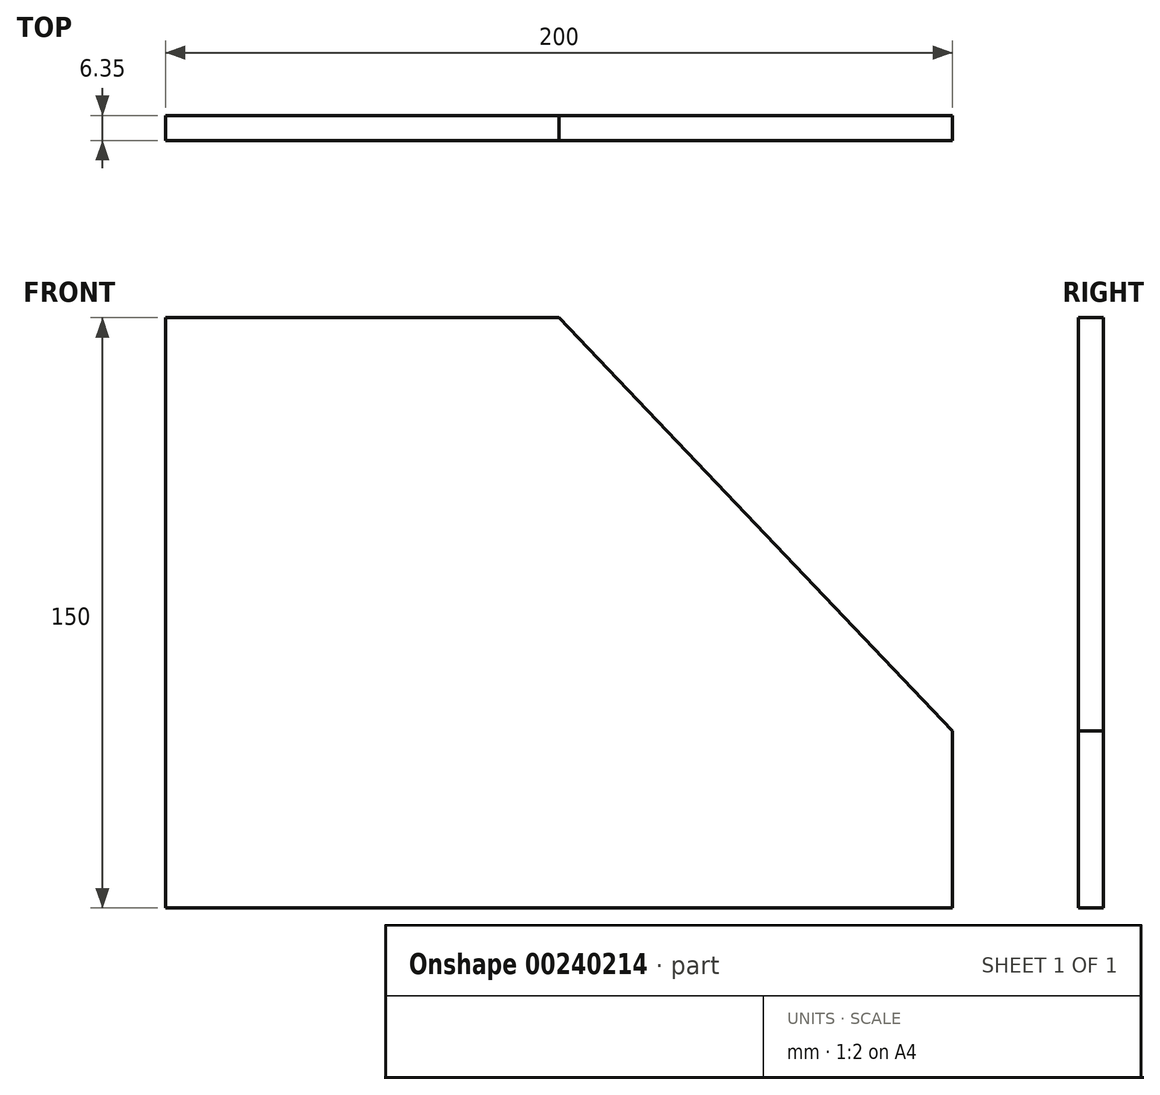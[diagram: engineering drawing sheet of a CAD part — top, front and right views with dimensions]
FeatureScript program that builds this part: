
annotation { "Feature Type Name" : "Feature", "Feature Type Description" : "" }
export const myFeature = defineFeature(function(context is Context, id is Id, definition is map)
    precondition{}
    {
        {
            var Q0;
            Q0=qCreatedBy(makeId("Front.planeOp"),FACE);
            var sketch = newSketch(context, id + "F0", { "sketchPlane" : qUnion([Q0])});
            skLineSegment(sketch, "E0.bottom", {"start": v(0, 0) * mm, "end": v(200, 0) * mm});
            skLineSegment(sketch, "E0.top", {"start": v(0, 150) * mm, "end": v(100, 150) * mm});
            skLineSegment(sketch, "E0.left", {"start": v(0, 0) * mm, "end": v(0, 150) * mm});
            skLineSegment(sketch, "E0.right", {"start": v(200, 0) * mm, "end": v(200, 45) * mm});
            skPoint(sketch, "E1", {"position": v(200, 45) * mm});
            skPoint(sketch, "E2", {"position": v(100, 150) * mm});
            skLineSegment(sketch, "E3", {"start": v(200, 45) * mm, "end": v(100, 150) * mm});
            skPoint(sketch, "E4.orphan", {"position": v(200, 150) * mm});
            skSolve(sketch);
        }
        {
            var Q0;
            Q0 = qSketchRegion(id + "F0", true);
            extrude(context, id + "F1", {"entities" : qUnion([Q0]), "depth" : 6.35 * mm});
        }
    });
